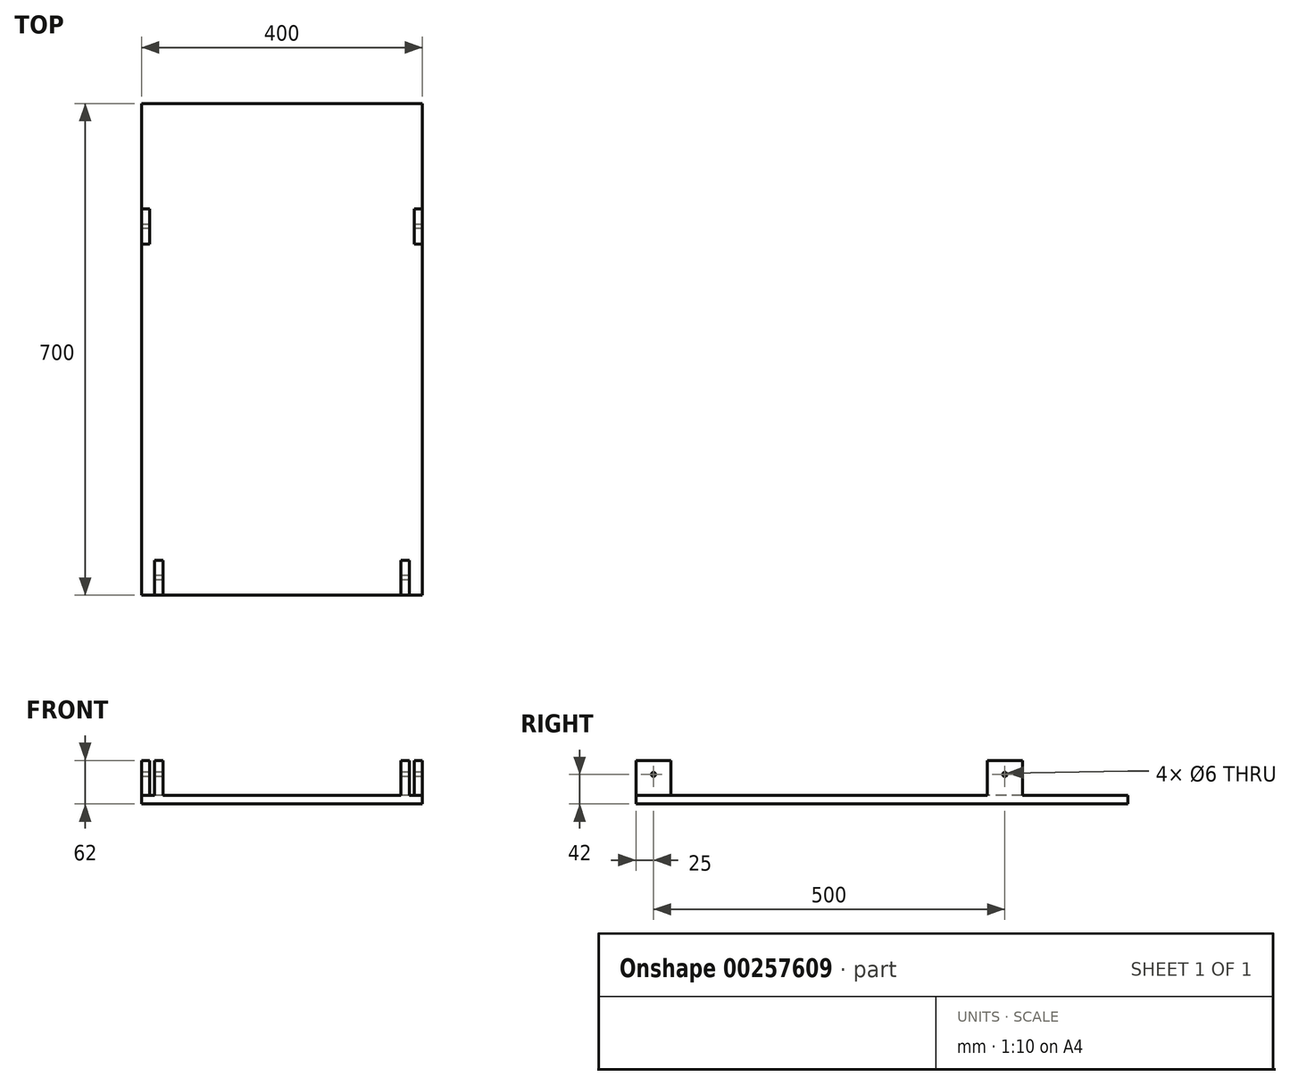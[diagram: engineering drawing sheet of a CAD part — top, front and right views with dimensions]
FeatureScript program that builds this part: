
annotation { "Feature Type Name" : "Feature", "Feature Type Description" : "" }
export const myFeature = defineFeature(function(context is Context, id is Id, definition is map)
    precondition{}
    {
        {
            var Q0;
            Q0=qCreatedBy(makeId("Front.planeOp"),FACE);
            var sketch = newSketch(context, id + "F0", { "sketchPlane" : qUnion([Q0])});
            skLineSegment(sketch, "E0.bottom", {"start": v(0, 0) * mm, "end": v(400, 0) * mm});
            skLineSegment(sketch, "E0.top", {"start": v(0, 12) * mm, "end": v(400, 12) * mm});
            skLineSegment(sketch, "E0.left", {"start": v(0, 0) * mm, "end": v(0, 12) * mm});
            skLineSegment(sketch, "E0.right", {"start": v(400, 0) * mm, "end": v(400, 12) * mm});
            skSolve(sketch);
        }
        {
            var Q0;
            Q0=makeQuery(id+"F0.imprint","IMPRINT",FACE,{"disambiguationData":[TD([[makeQuery(id+"F0.imprint","IMPRINT",EDGE,{"derivedFrom":sQuery(id+"F0.wireOp",EDGE,"E0.bottom")}),1.0]])]});
            extrude(context, id + "F1", {"entities" : qUnion([Q0]), "oppositeDirection" : true, "depth" : 700 * mm});
        }
        {
            var Q0;
            Q0=makeQuery(id+"F1.opExtrude","SWEPT_FACE",FACE,{"disambiguationData":[OSD([sQuery(id+"F0.wireOp",EDGE,"E0.top")])]});
            var sketch = newSketch(context, id + "F2", { "sketchPlane" : qUnion([Q0])});
            skLineSegment(sketch, "E1.bottom", {"start": v(31, 0) * mm, "end": v(19, 0) * mm});
            skLineSegment(sketch, "E1.top", {"start": v(31, 50) * mm, "end": v(19, 50) * mm});
            skLineSegment(sketch, "E1.left", {"start": v(31, 0) * mm, "end": v(31, 50) * mm});
            skLineSegment(sketch, "E1.right", {"start": v(19, 0) * mm, "end": v(19, 50) * mm});
            skLineSegment(sketch, "E2.bottom", {"start": v(381, 0) * mm, "end": v(369, 0) * mm});
            skLineSegment(sketch, "E2.top", {"start": v(381, 50) * mm, "end": v(369, 50) * mm});
            skLineSegment(sketch, "E2.left", {"start": v(381, 0) * mm, "end": v(381, 50) * mm});
            skLineSegment(sketch, "E2.right", {"start": v(369, 0) * mm, "end": v(369, 50) * mm});
            skLineSegment(sketch, "E3.bottom", {"start": v(0, 550) * mm, "end": v(12, 550) * mm});
            skLineSegment(sketch, "E3.top", {"start": v(0, 500) * mm, "end": v(12, 500) * mm});
            skLineSegment(sketch, "E3.left", {"start": v(0, 550) * mm, "end": v(0, 500) * mm});
            skLineSegment(sketch, "E3.right", {"start": v(12, 550) * mm, "end": v(12, 500) * mm});
            skLineSegment(sketch, "E4.bottom", {"start": v(388, 550) * mm, "end": v(400, 550) * mm});
            skLineSegment(sketch, "E4.top", {"start": v(388, 500) * mm, "end": v(400, 500) * mm});
            skLineSegment(sketch, "E4.left", {"start": v(388, 550) * mm, "end": v(388, 500) * mm});
            skLineSegment(sketch, "E4.right", {"start": v(400, 550) * mm, "end": v(400, 500) * mm});
            skSolve(sketch);
        }
        {
            var Q0;
            Q0 = qSketchRegion(id + "F2", true);
            extrude(context, id + "F3", {"entities" : qUnion([Q0]), "operationType" : NewBodyOperationType.ADD, "depth" : 50 * mm});
        }
        {
            var Q0;
            Q0=makeQuery(id+"F3.opExtrude","SWEPT_FACE",FACE,{"disambiguationData":[OSD([sQuery(id+"F2.wireOp",EDGE,"E1.right")])]});
            var sketch = newSketch(context, id + "F4", { "sketchPlane" : qUnion([Q0])});
            skCircle(sketch, "E5", {"center": v(-25, 42) * mm, "radius": 3 * mm});
            skCircle(sketch, "E6", {"center": v(-525, 42) * mm, "radius": 3 * mm});
            skSolve(sketch);
        }
        {
            var Q0;
            Q0 = qSketchRegion(id + "F4", true);
            extrude(context, id + "F5", {"entities" : qUnion([Q0]), "operationType" : NewBodyOperationType.REMOVE, "endBound" : BoundingType.THROUGH_ALL, "oppositeDirection" : true, "depth" : 25 * mm, "hasSecondDirection" : true, "secondDirectionBound" : SecondDirectionBoundingType.THROUGH_ALL, "secondDirectionOppositeDirection" : false, "secondDirectionDepth" : 25 * mm});
        }
    });
